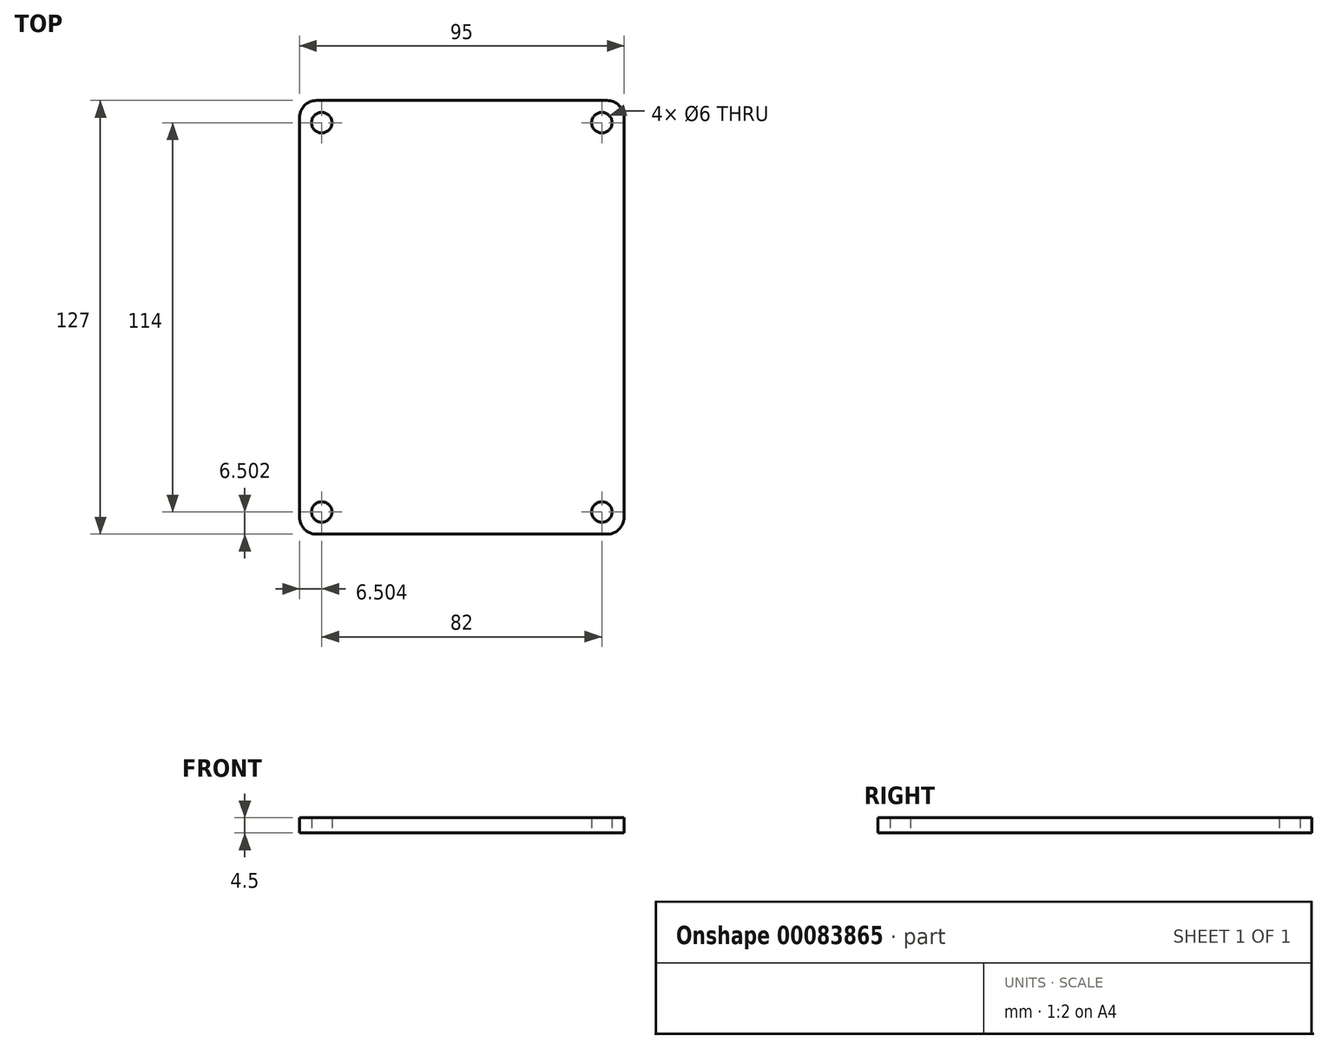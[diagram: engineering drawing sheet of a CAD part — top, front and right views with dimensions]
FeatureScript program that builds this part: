
annotation { "Feature Type Name" : "Feature", "Feature Type Description" : "" }
export const myFeature = defineFeature(function(context is Context, id is Id, definition is map)
    precondition{}
    {
        {
            var Q0;
            Q0=qCreatedBy(makeId("Top.planeOp"),FACE);
            var sketch = newSketch(context, id + "F0", { "sketchPlane" : qUnion([Q0])});
            skLineSegment(sketch, "E0.bottom", {"start": v(-56.13, 82.02) * mm, "end": v(28.87, 82.02) * mm});
            skLineSegment(sketch, "E0.top", {"start": v(-56.13, -44.98) * mm, "end": v(28.87, -44.98) * mm});
            skLineSegment(sketch, "E0.left", {"start": v(-61.13, 77.02) * mm, "end": v(-61.13, -39.98) * mm});
            skLineSegment(sketch, "E0.right", {"start": v(33.87, 77.02) * mm, "end": v(33.87, -39.98) * mm});
            skPoint(sketch, "E1.visualSharp", {"position": v(33.87, 82.02) * mm});
            skArc(sketch, "E1.filletArc", {"start": v(33.87, 77.02) * mm, "mid": v(32.4, 80.56) * mm, "end": v(28.87, 82.02) * mm});
            skPoint(sketch, "E2.visualSharp", {"position": v(-61.13, 82.02) * mm});
            skArc(sketch, "E2.filletArc", {"start": v(-56.13, 82.02) * mm, "mid": v(-59.66, 80.56) * mm, "end": v(-61.13, 77.02) * mm});
            skPoint(sketch, "E3.visualSharp", {"position": v(33.87, -44.98) * mm});
            skArc(sketch, "E3.filletArc", {"start": v(28.87, -44.98) * mm, "mid": v(32.4, -43.51) * mm, "end": v(33.87, -39.98) * mm});
            skPoint(sketch, "E4.visualSharp", {"position": v(-61.13, -44.98) * mm});
            skArc(sketch, "E4.filletArc", {"start": v(-61.13, -39.98) * mm, "mid": v(-59.66, -43.51) * mm, "end": v(-56.13, -44.98) * mm});
            skCircle(sketch, "E5", {"center": v(-54.63, 75.52) * mm, "radius": 3 * mm});
            skCircle(sketch, "E6", {"center": v(27.37, 75.52) * mm, "radius": 3 * mm});
            skCircle(sketch, "E7", {"center": v(27.37, -38.48) * mm, "radius": 3 * mm});
            skCircle(sketch, "E8", {"center": v(-54.63, -38.48) * mm, "radius": 3 * mm});
            skSolve(sketch);
        }
        {
            var Q0;
            Q0 = qSketchRegion(id + "F0", true);
            extrude(context, id + "F1", {"entities" : qUnion([Q0]), "depth" : 4.5 * mm});
        }
    });
